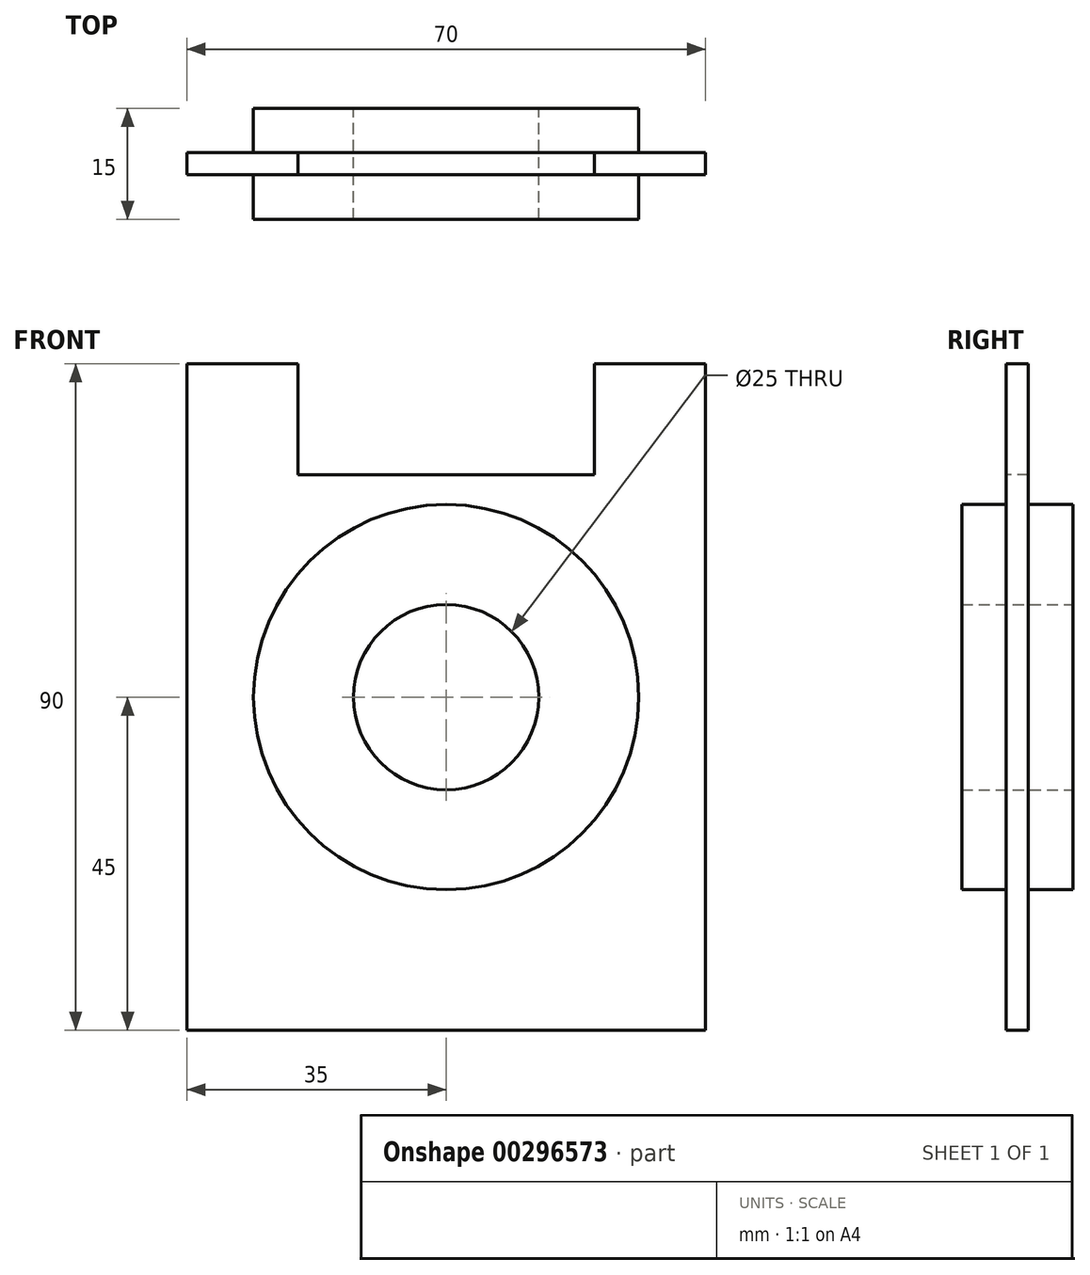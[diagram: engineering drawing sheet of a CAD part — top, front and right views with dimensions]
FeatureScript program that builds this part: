
annotation { "Feature Type Name" : "Feature", "Feature Type Description" : "" }
export const myFeature = defineFeature(function(context is Context, id is Id, definition is map)
    precondition{}
    {
        {
            var Q0;
            Q0=qCreatedBy(makeId("Front.planeOp"),FACE);
            var sketch = newSketch(context, id + "F0", { "sketchPlane" : qUnion([Q0])});
            skLineSegment(sketch, "E0.bottom", {"start": v(35, 45) * mm, "end": v(-35, 45) * mm});
            skLineSegment(sketch, "E0.top", {"start": v(35, -45) * mm, "end": v(-35, -45) * mm});
            skLineSegment(sketch, "E0.left", {"start": v(35, 45) * mm, "end": v(35, -45) * mm});
            skLineSegment(sketch, "E0.right", {"start": v(-35, 45) * mm, "end": v(-35, -45) * mm});
            skPoint(sketch, "E0.middle", {"position": v(0, 0) * mm});
            skSolve(sketch);
        }
        {
            var Q0;
            Q0=makeQuery(id+"F0.imprint","IMPRINT",FACE,{"disambiguationData":[TD([[makeQuery(id+"F0.imprint","IMPRINT",EDGE,{"derivedFrom":sQuery(id+"F0.wireOp",EDGE,"E0.bottom")}),1.0]])]});
            extrude(context, id + "F1", {"entities" : qUnion([Q0]), "depth" : 3 * mm});
        }
        {
            var Q0;
            Q0=sQuery(id+"F0.wireOp",VERTEX,"E0.middle");
            var Q1;
            Q1=makeQuery(id+"F1.opExtrude","SWEPT_BODY",BODY,{"disambiguationData":[OSD([sQuery(id+"F0.wireOp",EDGE,"E0.bottom"),sQuery(id+"F0.wireOp",EDGE,"E0.top"),sQuery(id+"F0.wireOp",EDGE,"E0.left"),sQuery(id+"F0.wireOp",EDGE,"E0.right")])]});
            hole(context, id + "F2", {"style" : HoleStyle.SIMPLE, "endStyle" : HoleEndStyle.THROUGH, "oppositeDirection" : true, "holeDiameter" : 52 * mm, "tappedDepth" : 12 * mm, "tapClearance" : 3, "locations" : qUnion([Q0]), "scope" : qUnion([Q1])});
        }
        {
            var Q0;
            Q0=qCreatedBy(makeId("Front.planeOp"),FACE);
            var sketch = newSketch(context, id + "F3", { "sketchPlane" : qUnion([Q0])});
            skCircle(sketch, "E1", {"center": v(0, 0) * mm, "radius": 26 * mm});
            skCircle(sketch, "E2", {"center": v(0, 0) * mm, "radius": 12.5 * mm});
            skSolve(sketch);
        }
        {
            var Q0;
            Q0=makeQuery(id+"F3.imprint","IMPRINT",FACE,{"disambiguationData":[TD([[makeQuery(id+"F3.imprint","IMPRINT",EDGE,{"derivedFrom":sQuery(id+"F3.wireOp",EDGE,"E1")}),1.0]])]});
            extrude(context, id + "F4", {"entities" : qUnion([Q0]), "operationType" : NewBodyOperationType.ADD, "depth" : 9 * mm, "hasSecondDirection" : true, "secondDirectionOppositeDirection" : true, "secondDirectionDepth" : 6 * mm});
        }
        {
            var Q0;
            Q0=makeQuery(id+"F1.opExtrude","CAP_FACE",FACE,{"disambiguationData":[OSD([sQuery(id+"F0.wireOp",EDGE,"E0.bottom"),sQuery(id+"F0.wireOp",EDGE,"E0.top"),sQuery(id+"F0.wireOp",EDGE,"E0.left"),sQuery(id+"F0.wireOp",EDGE,"E0.right")])],"isStart":false});
            var sketch = newSketch(context, id + "F5", { "sketchPlane" : qUnion([Q0])});
            skLineSegment(sketch, "E3", {"start": v(-35, 45) * mm, "end": v(-20, 45) * mm});
            skLineSegment(sketch, "E4", {"start": v(-20, 45) * mm, "end": v(20, 45) * mm});
            skLineSegment(sketch, "E5", {"start": v(20, 45) * mm, "end": v(35, 45) * mm});
            skLineSegment(sketch, "E6", {"start": v(-20, 45) * mm, "end": v(-20, 30) * mm});
            skLineSegment(sketch, "E7", {"start": v(-20, 30) * mm, "end": v(20, 30) * mm});
            skLineSegment(sketch, "E8", {"start": v(20, 30) * mm, "end": v(20, 45) * mm});
            skSolve(sketch);
        }
        {
            var Q0;
            Q0=makeQuery(id+"F5.imprint","IMPRINT",FACE,{"disambiguationData":[TD([[makeQuery(id+"F5.imprint","IMPRINT",EDGE,{"derivedFrom":sQuery(id+"F5.wireOp",EDGE,"E4")}),1.0]])]});
            extrude(context, id + "F6", {"entities" : qUnion([Q0]), "operationType" : NewBodyOperationType.REMOVE, "oppositeDirection" : true, "depth" : 25 * mm});
        }
    });
